# Revit family: Table-Teknion-ZNQS_Add_On_Tablet-R2022
name_source: partatom
category: Furniture
units: mm (PartAtom-declared; Revit-internal decimal feet)

## family parameters
Always vertical = Yes
Cut with Voids When Loaded = No
Enable Cutting in Views = No
OmniClass Number = 23.40.20.00
OmniClass Title = General Furniture and Specialties
Render Appearance Source = Family Geometry
Room Calculation Point = No
Shared = Yes
Work Plane-Based = No

## types (3) — shared parameters
Assembly Code = E2020200
Manufacturer = Teknion
Manufacturer Fax = 416.661.4586
Part Number = ZNQS
Product Documentation Link = https://www.teknion.com
Product Line = Modular Seating
Product Page URL = https://www.teknion.com
Series = Zones
Sustainability Data = https://www.teknion.com
URL = www.teknion.com
Unit Weight URL = http://www.teknion.com
Warranty = http://www.teknion.com
zero-valued in all types: Default Elevation

## per-type parameters (varying)
| type | Description | Model | Personal Tablet | Shared Tablet |
| Mid-Run Shared Tablet | Add-On Tablet, Shared, Mid-Run | ZNQSS | No | Yes |
| Mid-Run Personal Tablet | Add-On Tablet, Mid-Run – Personal | ZNQSM | Yes | No |
| End of Run Personal Tablet | Add-On Tablet, End of Run – Personal | ZNQSE | Yes | No |

## geometry (parser evidence)
native form markers: Sweep x3
no freeform markers — native parametric forms only
